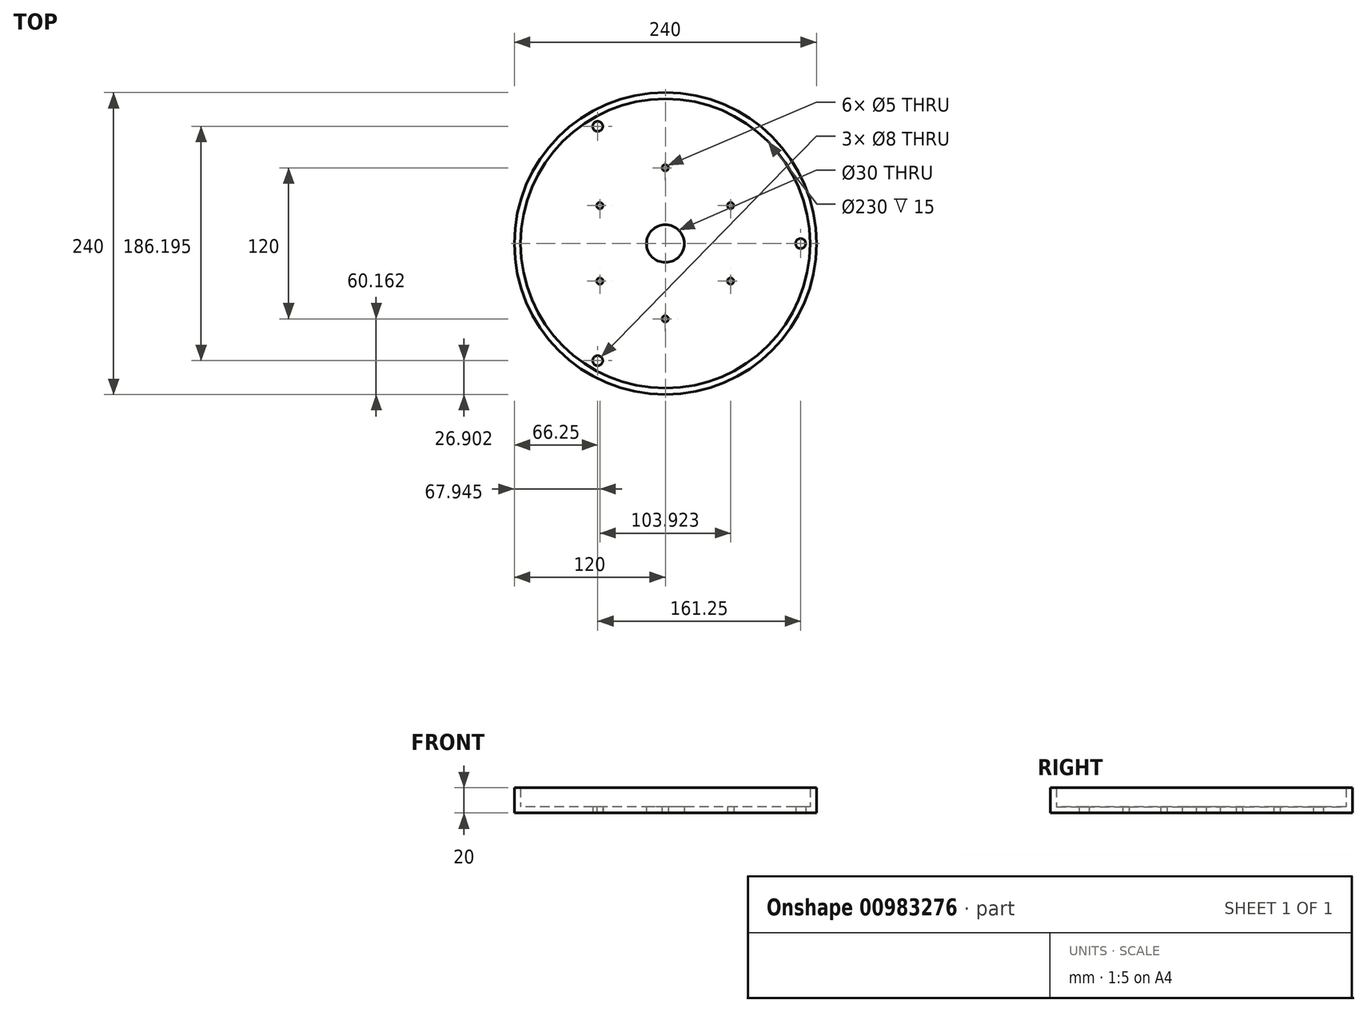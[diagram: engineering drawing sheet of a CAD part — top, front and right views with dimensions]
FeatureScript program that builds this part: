
annotation { "Feature Type Name" : "Feature", "Feature Type Description" : "" }
export const myFeature = defineFeature(function(context is Context, id is Id, definition is map)
    precondition{}
    {
        {
            var Q0;
            Q0=qCreatedBy(makeId("Top.planeOp"),FACE);
            var sketch = newSketch(context, id + "F0", { "sketchPlane" : qUnion([Q0])});
            skCircle(sketch, "E0", {"center": v(0, 0) * mm, "radius": 15 * mm});
            skCircle(sketch, "E1", {"center": v(0, 0) * mm, "radius": 115 * mm});
            skCircle(sketch, "E2", {"center": v(0, 0) * mm, "radius": 120 * mm});
            skCircle(sketch, "E3", {"center": v(51.87, -29.84) * mm, "radius": 2.5 * mm});
            skCircle(sketch, "E4", {"center": v(107.5, 0) * mm, "radius": 4 * mm});
            skCircle(sketch, "E5.1.0", {"center": v(51.87, 30.16) * mm, "radius": 2.5 * mm});
            skCircle(sketch, "E5.2.0", {"center": v(-0.1, 60.16) * mm, "radius": 2.5 * mm});
            skCircle(sketch, "E5.3.0", {"center": v(-52.05, 30.16) * mm, "radius": 2.5 * mm});
            skCircle(sketch, "E5.4.0", {"center": v(-52.05, -29.84) * mm, "radius": 2.5 * mm});
            skCircle(sketch, "E5.5.0", {"center": v(-0.1, -59.84) * mm, "radius": 2.5 * mm});
            skCircle(sketch, "E6.1.0", {"center": v(-53.75, 93.1) * mm, "radius": 4 * mm});
            skCircle(sketch, "E6.2.0", {"center": v(-53.75, -93.1) * mm, "radius": 4 * mm});
            skSolve(sketch);
        }
        {
            var Q0;
            Q0=makeQuery(id+"F0.imprint","IMPRINT",FACE,{"disambiguationData":[TD([[makeQuery(id+"F0.imprint","IMPRINT",EDGE,{"derivedFrom":sQuery(id+"F0.wireOp",EDGE,"E0")}),-1.0]])]});
            extrude(context, id + "F1", {"entities" : qUnion([Q0]), "depth" : 5 * mm, "offsetDistance" : 25 * mm});
        }
        {
            var Q0;
            Q0=makeQuery(id+"F0.imprint","IMPRINT",FACE,{"disambiguationData":[TD([[makeQuery(id+"F0.imprint","IMPRINT",EDGE,{"derivedFrom":sQuery(id+"F0.wireOp",EDGE,"E1")}),-1.0]])]});
            extrude(context, id + "F2", {"entities" : qUnion([Q0]), "operationType" : NewBodyOperationType.ADD, "depth" : 20 * mm, "offsetDistance" : 25 * mm});
        }
    });
